# Revit family: Patères
name_source: partatom
category: Appareils sanitaires
units: mm (PartAtom-declared; Revit-internal decimal feet)

## family parameters
Autoriser la découpe dans les vues = Non
Conserver l'orientation des annotations = Non
Cote de connecteur circulaire = Utiliser le diamètre
Couper avec des vides une fois chargée = Non
Hôte = Face
Numéro OmniClass = 23.40.00.00
Partagée = Non
Repère de localisation dans la pièce = Non
Titre OmniClass = Equipment and Furnishings
Type d'élément = Normal

## types (1)
- Patère simple
    BIMobject category = Sanitary Accessories
    BIMobject category code = sanitary-accessories1
    BIMobject main category = Sanitary
    BIMobject main category code = sanitary
    Brand url = http://www.hewi.com
    Design country = Germany
    Edition number = 1
    Elévation par défaut = 1219 mm
    IFC Classification = Sanitary Terminal
    Manufacturer country = Germany
    Manufacturer name = HEWI
    Material 1 = HEWI - 18 Mustard yellow
    Material main = Polyamide
    NBS Reference Code = 31-75
    NBS Reference Description = Sanitary Accessories
    Nominal height = 0 mm  [stored 0 ft]
    Nominal width = 0 mm  [stored 0 ft]
    OmniClass Code = 23-19 31 17
    OmniClass Description = Sanitary Room Units
    Product Guid = 40143210-a057-4f5a-abff-438334db2816
    Product SKU = 477-90-045
    Product data url = https://bimobject.com
    Product family = Sanitary
    Product group = Hooks, Walking aid holders
    Product url = https://catalog.hewi.com
    QR code = http://bimobject.com
    Technical description = https://catalog.hewi.com
    UNSPSC Code = 301815
    Uniclass 1.4 Code = L721
    Uniclass 1.4 Description = Sanitary equipment
    Uniclass 2.0 Code = PR-31-75
    Uniclass 2.0 Description = Sanitary Accessories

note: [stored X ft] marks values corroborated as IEEE doubles in the binary element streams (Revit-internal decimal feet)

## geometry (parser evidence)
native form markers: Sweep x4
no freeform markers — native parametric forms only
